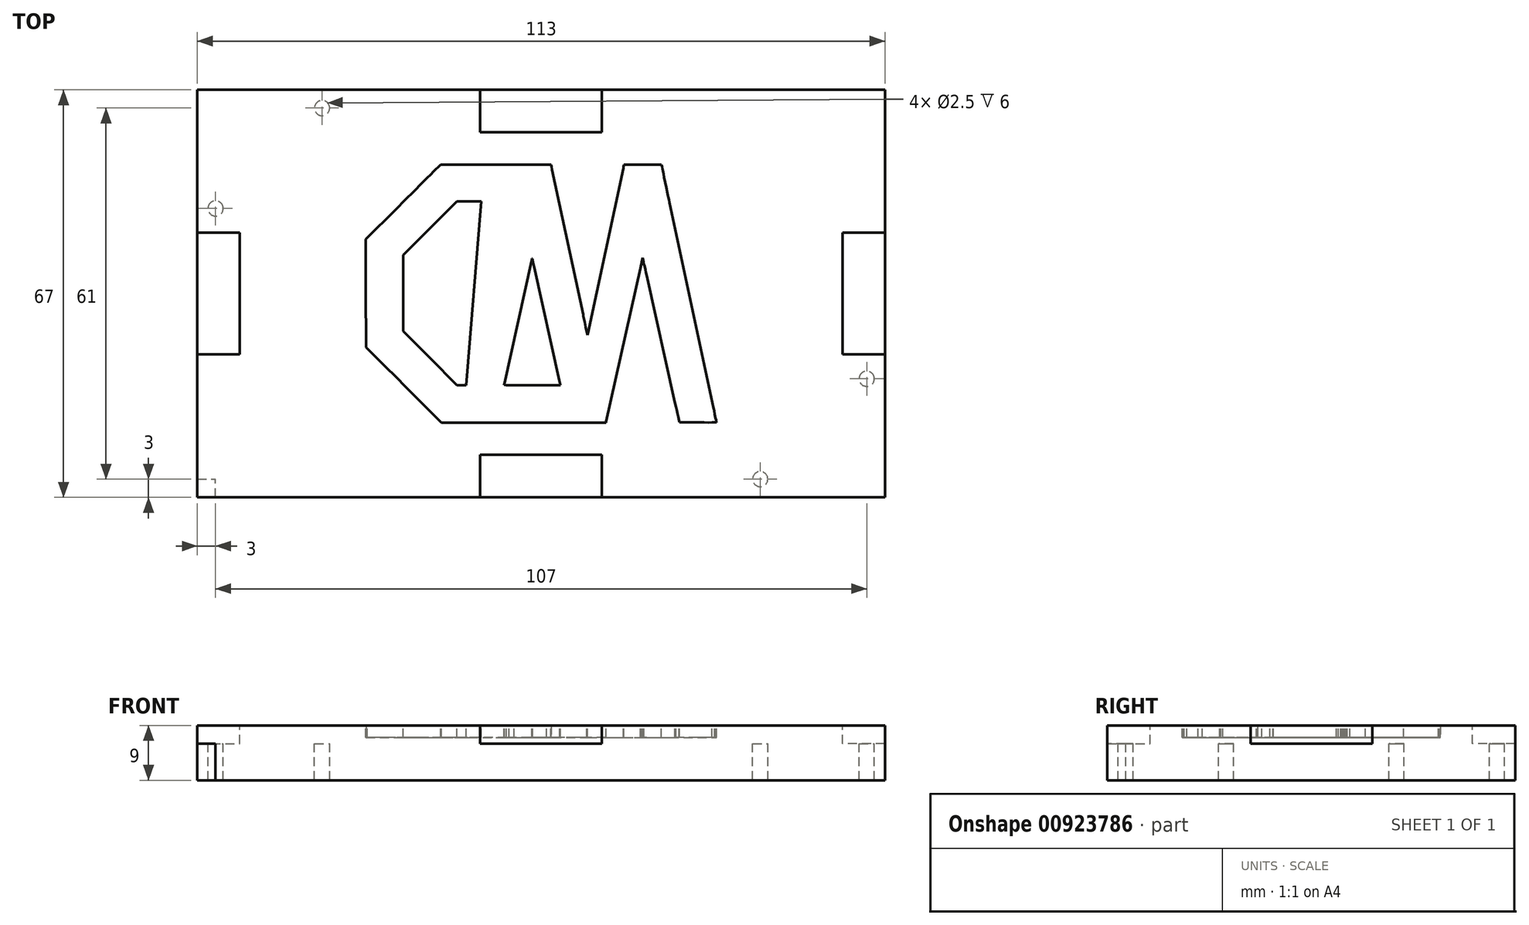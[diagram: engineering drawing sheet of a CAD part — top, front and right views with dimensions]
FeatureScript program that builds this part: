
annotation { "Feature Type Name" : "Feature", "Feature Type Description" : "" }
export const myFeature = defineFeature(function(context is Context, id is Id, definition is map)
    precondition{}
    {
        {
            var Q0;
            Q0=qCreatedBy(makeId("Top.planeOp"),FACE);
            var sketch = newSketch(context, id + "F0", { "sketchPlane" : qUnion([Q0])});
            skLineSegment(sketch, "E0.bottom", {"start": v(-56.5, 33.5) * mm, "end": v(56.5, 33.5) * mm});
            skLineSegment(sketch, "E0.top", {"start": v(-56.5, -33.5) * mm, "end": v(56.5, -33.5) * mm});
            skLineSegment(sketch, "E0.left", {"start": v(-56.5, 33.5) * mm, "end": v(-56.5, -33.5) * mm});
            skLineSegment(sketch, "E0.right", {"start": v(56.5, 33.5) * mm, "end": v(56.5, -33.5) * mm});
            skPoint(sketch, "E0.middle", {"position": v(0, 0) * mm});
            skSolve(sketch);
        }
        {
            var Q0;
            Q0=qSketchRegion(id+"F0",true);
            extrude(context, id + "F1", {"entities" : qUnion([Q0]), "depth" : 3 * mm, "offsetDistance" : 25 * mm});
        }
        {
            var Q0;
            Q0=makeQuery(id+"F1.opExtrude","CAP_FACE",FACE,{"disambiguationData":[OSD([sQuery(id+"F0.wireOp",EDGE,"E0.bottom"),sQuery(id+"F0.wireOp",EDGE,"E0.top"),sQuery(id+"F0.wireOp",EDGE,"E0.left"),sQuery(id+"F0.wireOp",EDGE,"E0.right")])],"isStart":true});
            var sketch = newSketch(context, id + "F2", { "sketchPlane" : qUnion([Q0])});
            skCircle(sketch, "E1", {"center": v(-36, 30.5) * mm, "radius": 1.25 * mm});
            skCircle(sketch, "E2.MirrorC", {"center": v(36, 30.5) * mm, "radius": 1.25 * mm});
            skCircle(sketch, "E3.MirrorC", {"center": v(-36, -30.5) * mm, "radius": 1.25 * mm});
            skCircle(sketch, "E4.MirrorC", {"center": v(36, -30.5) * mm, "radius": 1.25 * mm});
            skCircle(sketch, "E5", {"center": v(-53.5, 14) * mm, "radius": 1.25 * mm});
            skCircle(sketch, "E6.MirrorC", {"center": v(-53.5, -14) * mm, "radius": 1.25 * mm});
            skCircle(sketch, "E7.MirrorC", {"center": v(53.5, 14) * mm, "radius": 1.25 * mm});
            skCircle(sketch, "E8.MirrorC", {"center": v(53.5, -14) * mm, "radius": 1.25 * mm});
            skLineSegment(sketch, "E9", {"start": v(-56.5, 33.5) * mm, "end": v(-56.5, 30.5) * mm});
            skLineSegment(sketch, "E10.MirrorCS", {"start": v(56.5, 33.5) * mm, "end": v(56.5, 30.5) * mm});
            skLineSegment(sketch, "E11", {"start": v(-56.5, 30.5) * mm, "end": v(56.5, 30.5) * mm});
            skLineSegment(sketch, "E12", {"start": v(-56.5, 33.5) * mm, "end": v(-53.5, 33.5) * mm});
            skLineSegment(sketch, "E13.MirrorCS", {"start": v(-56.5, -33.5) * mm, "end": v(-53.5, -33.5) * mm});
            skLineSegment(sketch, "E14", {"start": v(-53.5, 33.5) * mm, "end": v(-53.5, -33.5) * mm});
            skSolve(sketch);
        }
        {
            var Q0;
            Q0=makeQuery(id+"F2.imprint","IMPRINT",FACE,{"disambiguationData":[TD([[makeQuery(id+"F2.imprint","IMPRINT",EDGE,{"derivedFrom":sQuery(id+"F2.wireOp",EDGE,"E5")}),1.0]])]});
            var Q1;
            Q1=makeQuery(id+"F2.imprint","IMPRINT",FACE,{"disambiguationData":[TD([[makeQuery(id+"F2.imprint","IMPRINT",EDGE,{"derivedFrom":sQuery(id+"F2.wireOp",EDGE,"E1")}),1.0]])]});
            var Q2;
            Q2=makeQuery(id+"F2.imprint","IMPRINT",FACE,{"disambiguationData":[TD([[makeQuery(id+"F2.imprint","IMPRINT",EDGE,{"derivedFrom":sQuery(id+"F2.wireOp",EDGE,"09FGcPzo-r08X-NdcF-ZMil-9gokYAyHGJ6w")}),1.0]])]});
            var Q3;
            Q3=makeQuery(id+"F2.imprint","IMPRINT",FACE,{"disambiguationData":[TD([[makeQuery(id+"F2.imprint","IMPRINT",EDGE,{"derivedFrom":sQuery(id+"F2.wireOp",EDGE,"6b634f44-071d-4c88-9b46-4b31445dddd10.MirrorC")}),-1.0]])]});
            var Q4;
            Q4=makeQuery(id+"F2.imprint","IMPRINT",FACE,{"disambiguationData":[TD([[makeQuery(id+"F2.imprint","IMPRINT",EDGE,{"derivedFrom":sQuery(id+"F2.wireOp",EDGE,"E2.MirrorC")}),-1.0]])]});
            var Q5;
            Q5=makeQuery(id+"F2.imprint","IMPRINT",FACE,{"disambiguationData":[TD([[makeQuery(id+"F2.imprint","IMPRINT",EDGE,{"derivedFrom":sQuery(id+"F2.wireOp",EDGE,"E7.MirrorC")}),-1.0]])]});
            var Q6;
            Q6=makeQuery(id+"F2.imprint","IMPRINT",FACE,{"disambiguationData":[TD([[makeQuery(id+"F2.imprint","IMPRINT",EDGE,{"derivedFrom":sQuery(id+"F2.wireOp",EDGE,"E8.MirrorC")}),1.0]])]});
            var Q7;
            Q7=makeQuery(id+"F2.imprint","IMPRINT",FACE,{"disambiguationData":[TD([[makeQuery(id+"F2.imprint","IMPRINT",EDGE,{"derivedFrom":sQuery(id+"F2.wireOp",EDGE,"E4.MirrorC")}),1.0]])]});
            var Q8;
            Q8=makeQuery(id+"F2.imprint","IMPRINT",FACE,{"disambiguationData":[TD([[makeQuery(id+"F2.imprint","IMPRINT",EDGE,{"derivedFrom":sQuery(id+"F2.wireOp",EDGE,"2bea74fb-fcac-444e-aa72-05c954cefff90.MirrorC")}),1.0]])]});
            var Q9;
            Q9=makeQuery(id+"F2.imprint","IMPRINT",FACE,{"disambiguationData":[TD([[makeQuery(id+"F2.imprint","IMPRINT",EDGE,{"derivedFrom":sQuery(id+"F2.wireOp",EDGE,"93892151-f29d-4d39-a853-46f32f35b9700.MirrorC")}),-1.0]])]});
            var Q10;
            Q10=makeQuery(id+"F2.imprint","IMPRINT",FACE,{"disambiguationData":[TD([[makeQuery(id+"F2.imprint","IMPRINT",EDGE,{"derivedFrom":sQuery(id+"F2.wireOp",EDGE,"E3.MirrorC")}),-1.0]])]});
            var Q11;
            Q11=makeQuery(id+"F2.imprint","IMPRINT",FACE,{"disambiguationData":[TD([[makeQuery(id+"F2.imprint","IMPRINT",EDGE,{"derivedFrom":sQuery(id+"F2.wireOp",EDGE,"E6.MirrorC")}),-1.0]])]});
            extrude(context, id + "F3", {"entities" : qUnion([Q0, Q1, Q2, Q3, Q4, Q5, Q6, Q7, Q8, Q9, Q10, Q11]), "operationType" : NewBodyOperationType.ADD, "depth" : 6 * mm, "offsetDistance" : 25 * mm});
        }
        {
            var Q0;
            Q0=makeQuery(id+"F1.opExtrude","CAP_FACE",FACE,{"disambiguationData":[OSD([sQuery(id+"F0.wireOp",EDGE,"E0.bottom"),sQuery(id+"F0.wireOp",EDGE,"E0.top"),sQuery(id+"F0.wireOp",EDGE,"E0.left"),sQuery(id+"F0.wireOp",EDGE,"E0.right")])],"isStart":false});
            var sketch = newSketch(context, id + "F4", { "sketchPlane" : qUnion([Q0])});
            skLineSegment(sketch, "E15", {"start": v(-10, 33.5) * mm, "end": v(10, 33.5) * mm});
            skLineSegment(sketch, "E16", {"start": v(-10, 33.5) * mm, "end": v(-10, 26.5) * mm});
            skLineSegment(sketch, "E17", {"start": v(-10, 26.5) * mm, "end": v(10, 26.5) * mm});
            skLineSegment(sketch, "E18", {"start": v(10, 26.5) * mm, "end": v(10, 33.5) * mm});
            skLineSegment(sketch, "E19.MirrorCS", {"start": v(-10, -33.5) * mm, "end": v(-10, -26.5) * mm});
            skLineSegment(sketch, "E20.MirrorCS", {"start": v(-10, -26.5) * mm, "end": v(10, -26.5) * mm});
            skLineSegment(sketch, "E21.MirrorCS", {"start": v(10, -26.5) * mm, "end": v(10, -33.5) * mm});
            skLineSegment(sketch, "E22.MirrorCS", {"start": v(-10, -33.5) * mm, "end": v(10, -33.5) * mm});
            skLineSegment(sketch, "E23", {"start": v(-56.5, 10) * mm, "end": v(-56.5, -10) * mm});
            skLineSegment(sketch, "E24", {"start": v(-56.5, 10) * mm, "end": v(-49.5, 10) * mm});
            skLineSegment(sketch, "E25", {"start": v(-49.5, 10) * mm, "end": v(-49.5, -10) * mm});
            skLineSegment(sketch, "E26", {"start": v(-49.5, -10) * mm, "end": v(-56.5, -10) * mm});
            skLineSegment(sketch, "E27.MirrorCS", {"start": v(56.5, 10) * mm, "end": v(49.5, 10) * mm});
            skLineSegment(sketch, "E28.MirrorCS", {"start": v(56.5, 10) * mm, "end": v(56.5, -10) * mm});
            skLineSegment(sketch, "E29.MirrorCS", {"start": v(49.5, -10) * mm, "end": v(56.5, -10) * mm});
            skLineSegment(sketch, "E30.MirrorCS", {"start": v(49.5, 10) * mm, "end": v(49.5, -10) * mm});
            skSolve(sketch);
        }
        {
            var Q0;
            Q0=makeQuery(id+"F4.imprint","IMPRINT",FACE,{"disambiguationData":[TD([[makeQuery(id+"F4.imprint","IMPRINT",EDGE,{"derivedFrom":sQuery(id+"F4.wireOp",EDGE,"E23")}),1.0]])]});
            var Q1;
            Q1=makeQuery(id+"F4.imprint","IMPRINT",FACE,{"disambiguationData":[TD([[makeQuery(id+"F4.imprint","IMPRINT",EDGE,{"derivedFrom":sQuery(id+"F4.wireOp",EDGE,"E15")}),-1.0]])]});
            var Q2;
            Q2=makeQuery(id+"F4.imprint","IMPRINT",FACE,{"disambiguationData":[TD([[makeQuery(id+"F4.imprint","IMPRINT",EDGE,{"derivedFrom":sQuery(id+"F4.wireOp",EDGE,"E27.MirrorCS")}),1.0]])]});
            var Q3;
            Q3=makeQuery(id+"F4.imprint","IMPRINT",FACE,{"disambiguationData":[TD([[makeQuery(id+"F4.imprint","IMPRINT",EDGE,{"derivedFrom":sQuery(id+"F4.wireOp",EDGE,"E19.MirrorCS")}),-1.0]])]});
            extrude(context, id + "F5", {"entities" : qUnion([Q0, Q1, Q2, Q3]), "operationType" : NewBodyOperationType.REMOVE, "oppositeDirection" : true, "depth" : 3 * mm, "offsetDistance" : 25 * mm});
        }
        {
            var Q0;
            Q0=makeQuery(id+"F1.opExtrude","CAP_FACE",FACE,{"disambiguationData":[OSD([sQuery(id+"F0.wireOp",EDGE,"E0.bottom"),sQuery(id+"F0.wireOp",EDGE,"E0.top"),sQuery(id+"F0.wireOp",EDGE,"E0.left"),sQuery(id+"F0.wireOp",EDGE,"E0.right")])],"isStart":false});
            var sketch = newSketch(context, id + "F6", { "sketchPlane" : qUnion([Q0])});
            skLineSegment(sketch, "E31", {"start": v(-13.82, -15.06) * mm, "end": v(-12.3, -15.06) * mm});
            skLineSegment(sketch, "E32", {"start": v(-18.24, -10.63) * mm, "end": v(-13.82, -15.06) * mm});
            skLineSegment(sketch, "E33", {"start": v(-22.67, -6.2) * mm, "end": v(-18.24, -10.63) * mm});
            skLineSegment(sketch, "E34", {"start": v(-22.67, -6.2) * mm, "end": v(-22.66, 6.32) * mm});
            skLineSegment(sketch, "E35", {"start": v(-18.26, 10.74) * mm, "end": v(-22.66, 6.32) * mm});
            skLineSegment(sketch, "E36", {"start": v(-13.86, 15.17) * mm, "end": v(-18.26, 10.74) * mm});
            skLineSegment(sketch, "E37", {"start": v(-9.85, 15.17) * mm, "end": v(-13.86, 15.17) * mm});
            skLineSegment(sketch, "E38", {"start": v(-12.3, -15.06) * mm, "end": v(-9.85, 15.17) * mm});
            skLineSegment(sketch, "E39", {"start": v(-6.04, -14.81) * mm, "end": v(-6.07, -14.95) * mm});
            skLineSegment(sketch, "E40", {"start": v(-6.07, -14.95) * mm, "end": v(-6.08, -15.01) * mm});
            skLineSegment(sketch, "E41", {"start": v(-6.04, -14.81) * mm, "end": v(-1.56, 5.34) * mm});
            skLineSegment(sketch, "E42", {"start": v(-1.5, 5.66) * mm, "end": v(-1.53, 5.51) * mm});
            skLineSegment(sketch, "E43", {"start": v(-1.53, 5.51) * mm, "end": v(-1.56, 5.34) * mm});
            skLineSegment(sketch, "E44", {"start": v(-1.4, 5.57) * mm, "end": v(-1.44, 5.72) * mm});
            skLineSegment(sketch, "E45", {"start": v(-1.44, 5.72) * mm, "end": v(-1.48, 5.78) * mm});
            skLineSegment(sketch, "E46", {"start": v(-1.48, 5.78) * mm, "end": v(-1.49, 5.78) * mm});
            skLineSegment(sketch, "E47", {"start": v(-1.49, 5.78) * mm, "end": v(-1.5, 5.76) * mm});
            skLineSegment(sketch, "E48", {"start": v(-1.5, 5.76) * mm, "end": v(-1.5, 5.66) * mm});
            skLineSegment(sketch, "E49", {"start": v(-1.14, 4.4) * mm, "end": v(-1.3, 5.12) * mm});
            skLineSegment(sketch, "E50", {"start": v(-1.3, 5.12) * mm, "end": v(-1.4, 5.57) * mm});
            skLineSegment(sketch, "E51", {"start": v(3, -14.3) * mm, "end": v(-1.14, 4.4) * mm});
            skLineSegment(sketch, "E52", {"start": v(3.13, -14.84) * mm, "end": v(3.06, -14.55) * mm});
            skLineSegment(sketch, "E53", {"start": v(3.06, -14.55) * mm, "end": v(3, -14.3) * mm});
            skLineSegment(sketch, "E54", {"start": v(3.19, -15.06) * mm, "end": v(3.13, -14.84) * mm});
            skLineSegment(sketch, "E55", {"start": v(0.11, -15.06) * mm, "end": v(3.19, -15.06) * mm});
            skLineSegment(sketch, "E56", {"start": v(-3.62, -15.07) * mm, "end": v(-3.3, -15.07) * mm});
            skLineSegment(sketch, "E57", {"start": v(-3.3, -15.07) * mm, "end": v(-2.73, -15.07) * mm});
            skLineSegment(sketch, "E58", {"start": v(-2.73, -15.07) * mm, "end": v(-2, -15.06) * mm});
            skLineSegment(sketch, "E59", {"start": v(-2, -15.06) * mm, "end": v(-1, -15.06) * mm});
            skLineSegment(sketch, "E60", {"start": v(-1, -15.06) * mm, "end": v(0.11, -15.06) * mm});
            skLineSegment(sketch, "E61", {"start": v(-6.08, -15.01) * mm, "end": v(-6.07, -15.02) * mm});
            skLineSegment(sketch, "E62", {"start": v(-6.07, -15.02) * mm, "end": v(-6.06, -15.02) * mm});
            skLineSegment(sketch, "E63", {"start": v(-6.06, -15.02) * mm, "end": v(-6.02, -15.03) * mm});
            skLineSegment(sketch, "E64", {"start": v(-6.02, -15.03) * mm, "end": v(-5.73, -15.05) * mm});
            skLineSegment(sketch, "E65", {"start": v(-5.73, -15.05) * mm, "end": v(-5.27, -15.07) * mm});
            skLineSegment(sketch, "E66", {"start": v(-5.27, -15.07) * mm, "end": v(-4.47, -15.08) * mm});
            skLineSegment(sketch, "E67", {"start": v(-4.47, -15.08) * mm, "end": v(-3.62, -15.07) * mm});
            skLineSegment(sketch, "E68", {"start": v(16.62, 5.68) * mm, "end": v(16.57, 5.4) * mm});
            skLineSegment(sketch, "E69", {"start": v(16.57, 5.4) * mm, "end": v(16.53, 5.24) * mm});
            skLineSegment(sketch, "E70", {"start": v(16.7, 5.9) * mm, "end": v(16.7, 5.91) * mm});
            skLineSegment(sketch, "E71", {"start": v(16.7, 5.91) * mm, "end": v(16.69, 5.91) * mm});
            skLineSegment(sketch, "E72", {"start": v(16.69, 5.91) * mm, "end": v(16.68, 5.9) * mm});
            skLineSegment(sketch, "E73", {"start": v(16.68, 5.9) * mm, "end": v(16.62, 5.68) * mm});
            skLineSegment(sketch, "E74", {"start": v(16.8, 5.5) * mm, "end": v(16.73, 5.8) * mm});
            skLineSegment(sketch, "E75", {"start": v(16.73, 5.8) * mm, "end": v(16.7, 5.88) * mm});
            skLineSegment(sketch, "E76", {"start": v(16.7, 5.88) * mm, "end": v(16.7, 5.9) * mm});
            skLineSegment(sketch, "E77", {"start": v(16.7, 5.9) * mm, "end": v(16.7, 5.9) * mm});
            skLineSegment(sketch, "E78", {"start": v(16.93, 4.84) * mm, "end": v(16.85, 5.19) * mm});
            skLineSegment(sketch, "E79", {"start": v(16.85, 5.19) * mm, "end": v(16.8, 5.5) * mm});
            skLineSegment(sketch, "E80", {"start": v(17.12, 3.95) * mm, "end": v(17, 4.52) * mm});
            skLineSegment(sketch, "E81", {"start": v(17, 4.52) * mm, "end": v(16.93, 4.84) * mm});
            skLineSegment(sketch, "E82", {"start": v(17.32, 3.06) * mm, "end": v(17.22, 3.5) * mm});
            skLineSegment(sketch, "E83", {"start": v(17.22, 3.5) * mm, "end": v(17.12, 3.95) * mm});
            skLineSegment(sketch, "E84", {"start": v(17.32, 3.06) * mm, "end": v(21.98, -17.92) * mm});
            skLineSegment(sketch, "E85", {"start": v(22.41, -19.78) * mm, "end": v(22.26, -19.1) * mm});
            skLineSegment(sketch, "E86", {"start": v(22.26, -19.1) * mm, "end": v(22.15, -18.6) * mm});
            skLineSegment(sketch, "E87", {"start": v(22.15, -18.6) * mm, "end": v(21.98, -17.92) * mm});
            skLineSegment(sketch, "E88", {"start": v(22.7, -21.07) * mm, "end": v(22.67, -20.91) * mm});
            skLineSegment(sketch, "E89", {"start": v(22.67, -20.91) * mm, "end": v(22.6, -20.61) * mm});
            skLineSegment(sketch, "E90", {"start": v(22.6, -20.61) * mm, "end": v(22.52, -20.26) * mm});
            skLineSegment(sketch, "E91", {"start": v(22.52, -20.26) * mm, "end": v(22.41, -19.78) * mm});
            skLineSegment(sketch, "E92", {"start": v(22.74, -21.18) * mm, "end": v(22.7, -21.07) * mm});
            skLineSegment(sketch, "E93", {"start": v(25.77, -21.19) * mm, "end": v(22.74, -21.18) * mm});
            skLineSegment(sketch, "E94", {"start": v(28.8, -21.11) * mm, "end": v(28.8, -21.14) * mm});
            skLineSegment(sketch, "E95", {"start": v(28.8, -21.14) * mm, "end": v(28.76, -21.16) * mm});
            skLineSegment(sketch, "E96", {"start": v(28.76, -21.16) * mm, "end": v(28.5, -21.18) * mm});
            skLineSegment(sketch, "E97", {"start": v(28.5, -21.18) * mm, "end": v(28.06, -21.2) * mm});
            skLineSegment(sketch, "E98", {"start": v(28.06, -21.2) * mm, "end": v(27.52, -21.2) * mm});
            skLineSegment(sketch, "E99", {"start": v(27.52, -21.2) * mm, "end": v(26.77, -21.2) * mm});
            skLineSegment(sketch, "E100", {"start": v(26.77, -21.2) * mm, "end": v(25.77, -21.19) * mm});
            skLineSegment(sketch, "E101", {"start": v(28.74, -20.79) * mm, "end": v(28.8, -21) * mm});
            skLineSegment(sketch, "E102", {"start": v(28.8, -21) * mm, "end": v(28.8, -21.11) * mm});
            skLineSegment(sketch, "E103", {"start": v(28.53, -19.8) * mm, "end": v(28.67, -20.46) * mm});
            skLineSegment(sketch, "E104", {"start": v(28.67, -20.46) * mm, "end": v(28.74, -20.79) * mm});
            skLineSegment(sketch, "E105", {"start": v(28.32, -18.79) * mm, "end": v(28.36, -18.98) * mm});
            skLineSegment(sketch, "E106", {"start": v(28.36, -18.98) * mm, "end": v(28.42, -19.26) * mm});
            skLineSegment(sketch, "E107", {"start": v(28.42, -19.26) * mm, "end": v(28.53, -19.8) * mm});
            skLineSegment(sketch, "E108", {"start": v(21.1, 14.95) * mm, "end": v(28.32, -18.79) * mm});
            skLineSegment(sketch, "E109", {"start": v(20.9, 15.85) * mm, "end": v(21, 15.41) * mm});
            skLineSegment(sketch, "E110", {"start": v(21, 15.41) * mm, "end": v(21.1, 14.95) * mm});
            skLineSegment(sketch, "E111", {"start": v(20.79, 16.43) * mm, "end": v(20.85, 16.1) * mm});
            skLineSegment(sketch, "E112", {"start": v(20.85, 16.1) * mm, "end": v(20.9, 15.85) * mm});
            skLineSegment(sketch, "E113", {"start": v(20.1, 19.65) * mm, "end": v(20.21, 19.1) * mm});
            skLineSegment(sketch, "E114", {"start": v(20.21, 19.1) * mm, "end": v(20.39, 18.3) * mm});
            skLineSegment(sketch, "E115", {"start": v(20.39, 18.3) * mm, "end": v(20.57, 17.45) * mm});
            skLineSegment(sketch, "E116", {"start": v(20.57, 17.45) * mm, "end": v(20.79, 16.43) * mm});
            skLineSegment(sketch, "E117", {"start": v(19.97, 20.25) * mm, "end": v(20.04, 19.92) * mm});
            skLineSegment(sketch, "E118", {"start": v(20.04, 19.92) * mm, "end": v(20.1, 19.65) * mm});
            skLineSegment(sketch, "E119", {"start": v(19.85, 20.87) * mm, "end": v(19.92, 20.5) * mm});
            skLineSegment(sketch, "E120", {"start": v(19.92, 20.5) * mm, "end": v(19.97, 20.25) * mm});
            skLineSegment(sketch, "E121", {"start": v(19.78, 21.22) * mm, "end": v(19.85, 20.87) * mm});
            skLineSegment(sketch, "E122", {"start": v(13.61, 21.22) * mm, "end": v(19.78, 21.22) * mm});
            skLineSegment(sketch, "E123", {"start": v(13.58, 21.06) * mm, "end": v(13.61, 21.22) * mm});
            skLineSegment(sketch, "E124", {"start": v(13.5, 20.65) * mm, "end": v(13.55, 20.9) * mm});
            skLineSegment(sketch, "E125", {"start": v(13.55, 20.9) * mm, "end": v(13.58, 21.06) * mm});
            skLineSegment(sketch, "E126", {"start": v(7.67, -6.57) * mm, "end": v(13.5, 20.65) * mm});
            skLineSegment(sketch, "E127", {"start": v(7.61, -6.83) * mm, "end": v(7.67, -6.57) * mm});
            skLineSegment(sketch, "E128", {"start": v(7.56, -6.55) * mm, "end": v(7.61, -6.83) * mm});
            skLineSegment(sketch, "E129", {"start": v(7.45, -6.02) * mm, "end": v(7.51, -6.32) * mm});
            skLineSegment(sketch, "E130", {"start": v(7.51, -6.32) * mm, "end": v(7.56, -6.55) * mm});
            skLineSegment(sketch, "E131", {"start": v(7.33, -5.45) * mm, "end": v(7.4, -5.79) * mm});
            skLineSegment(sketch, "E132", {"start": v(7.4, -5.79) * mm, "end": v(7.45, -6.02) * mm});
            skLineSegment(sketch, "E133", {"start": v(6.9, -3.42) * mm, "end": v(6.96, -3.71) * mm});
            skLineSegment(sketch, "E134", {"start": v(6.96, -3.71) * mm, "end": v(7.06, -4.18) * mm});
            skLineSegment(sketch, "E135", {"start": v(7.06, -4.18) * mm, "end": v(7.17, -4.72) * mm});
            skLineSegment(sketch, "E136", {"start": v(7.17, -4.72) * mm, "end": v(7.33, -5.45) * mm});
            skLineSegment(sketch, "E137", {"start": v(1.8, 20.35) * mm, "end": v(6.9, -3.42) * mm});
            skLineSegment(sketch, "E138", {"start": v(1.63, 21.19) * mm, "end": v(1.63, 21.18) * mm});
            skLineSegment(sketch, "E139", {"start": v(1.63, 21.18) * mm, "end": v(1.63, 21.17) * mm});
            skLineSegment(sketch, "E140", {"start": v(1.63, 21.17) * mm, "end": v(1.63, 21.15) * mm});
            skLineSegment(sketch, "E141", {"start": v(1.63, 21.15) * mm, "end": v(1.65, 21.07) * mm});
            skLineSegment(sketch, "E142", {"start": v(1.65, 21.07) * mm, "end": v(1.7, 20.87) * mm});
            skLineSegment(sketch, "E143", {"start": v(1.7, 20.87) * mm, "end": v(1.8, 20.35) * mm});
            skLineSegment(sketch, "E144", {"start": v(-7.44, 21.22) * mm, "end": v(0.91, 21.2) * mm});
            skLineSegment(sketch, "E145", {"start": v(0.91, 21.2) * mm, "end": v(1.58, 21.2) * mm});
            skLineSegment(sketch, "E146", {"start": v(1.58, 21.2) * mm, "end": v(1.62, 21.19) * mm});
            skLineSegment(sketch, "E147", {"start": v(1.62, 21.19) * mm, "end": v(1.63, 21.19) * mm});
            skLineSegment(sketch, "E148", {"start": v(1.63, 21.19) * mm, "end": v(1.63, 21.19) * mm});
            skLineSegment(sketch, "E149", {"start": v(-16.52, 21.22) * mm, "end": v(-7.44, 21.22) * mm});
            skLineSegment(sketch, "E150", {"start": v(-17.7, 20.03) * mm, "end": v(-16.52, 21.22) * mm});
            skLineSegment(sketch, "E151", {"start": v(-23.84, 13.88) * mm, "end": v(-22.32, 15.4) * mm});
            skLineSegment(sketch, "E152", {"start": v(-22.32, 15.4) * mm, "end": v(-20.88, 16.84) * mm});
            skLineSegment(sketch, "E153", {"start": v(-20.88, 16.84) * mm, "end": v(-19.6, 18.12) * mm});
            skLineSegment(sketch, "E154", {"start": v(-19.6, 18.12) * mm, "end": v(-18.76, 18.96) * mm});
            skLineSegment(sketch, "E155", {"start": v(-18.76, 18.96) * mm, "end": v(-18.12, 19.61) * mm});
            skLineSegment(sketch, "E156", {"start": v(-18.12, 19.61) * mm, "end": v(-17.7, 20.03) * mm});
            skLineSegment(sketch, "E157", {"start": v(-28.8, 8.92) * mm, "end": v(-23.84, 13.88) * mm});
            skLineSegment(sketch, "E158", {"start": v(-28.8, 0.04) * mm, "end": v(-28.8, 8.92) * mm});
            skLineSegment(sketch, "E159", {"start": v(-28.78, -8.84) * mm, "end": v(-28.78, -8.84) * mm});
            skLineSegment(sketch, "E160", {"start": v(-28.78, -8.84) * mm, "end": v(-28.78, -8.83) * mm});
            skLineSegment(sketch, "E161", {"start": v(-28.78, -8.83) * mm, "end": v(-28.78, -8.8) * mm});
            skLineSegment(sketch, "E162", {"start": v(-28.78, -8.8) * mm, "end": v(-28.8, -8.14) * mm});
            skLineSegment(sketch, "E163", {"start": v(-28.8, -8.14) * mm, "end": v(-28.8, 0.04) * mm});
            skLineSegment(sketch, "E164", {"start": v(-20.04, -17.54) * mm, "end": v(-22.15, -15.42) * mm});
            skLineSegment(sketch, "E165", {"start": v(-22.15, -15.42) * mm, "end": v(-23.96, -13.62) * mm});
            skLineSegment(sketch, "E166", {"start": v(-23.96, -13.62) * mm, "end": v(-25.46, -12.12) * mm});
            skLineSegment(sketch, "E167", {"start": v(-25.46, -12.12) * mm, "end": v(-26.67, -10.91) * mm});
            skLineSegment(sketch, "E168", {"start": v(-26.67, -10.91) * mm, "end": v(-27.6, -10) * mm});
            skLineSegment(sketch, "E169", {"start": v(-27.6, -10) * mm, "end": v(-28.25, -9.34) * mm});
            skLineSegment(sketch, "E170", {"start": v(-28.25, -9.34) * mm, "end": v(-28.57, -9.03) * mm});
            skLineSegment(sketch, "E171", {"start": v(-28.57, -9.03) * mm, "end": v(-28.74, -8.87) * mm});
            skLineSegment(sketch, "E172", {"start": v(-28.74, -8.87) * mm, "end": v(-28.77, -8.85) * mm});
            skLineSegment(sketch, "E173", {"start": v(-28.77, -8.85) * mm, "end": v(-28.78, -8.84) * mm});
            skLineSegment(sketch, "E174", {"start": v(-16.37, -21.22) * mm, "end": v(-20.04, -17.54) * mm});
            skLineSegment(sketch, "E175", {"start": v(-5.62, -21.22) * mm, "end": v(-16.37, -21.22) * mm});
            skLineSegment(sketch, "E176", {"start": v(7.88, -21.2) * mm, "end": v(6.99, -21.2) * mm});
            skLineSegment(sketch, "E177", {"start": v(6.99, -21.2) * mm, "end": v(5.64, -21.2) * mm});
            skLineSegment(sketch, "E178", {"start": v(5.64, -21.2) * mm, "end": v(3.9, -21.21) * mm});
            skLineSegment(sketch, "E179", {"start": v(3.9, -21.21) * mm, "end": v(1.87, -21.21) * mm});
            skLineSegment(sketch, "E180", {"start": v(1.87, -21.21) * mm, "end": v(-1.75, -21.22) * mm});
            skLineSegment(sketch, "E181", {"start": v(-1.75, -21.22) * mm, "end": v(-5.62, -21.22) * mm});
            skLineSegment(sketch, "E182", {"start": v(10.64, -21.2) * mm, "end": v(7.88, -21.2) * mm});
            skLineSegment(sketch, "E183", {"start": v(10.68, -21.04) * mm, "end": v(10.64, -21.2) * mm});
            skLineSegment(sketch, "E184", {"start": v(10.68, -21.04) * mm, "end": v(16.32, 4.16) * mm});
            skLineSegment(sketch, "E185", {"start": v(16.45, 4.82) * mm, "end": v(16.38, 4.47) * mm});
            skLineSegment(sketch, "E186", {"start": v(16.38, 4.47) * mm, "end": v(16.32, 4.16) * mm});
            skLineSegment(sketch, "E187", {"start": v(16.53, 5.24) * mm, "end": v(16.48, 5.02) * mm});
            skLineSegment(sketch, "E188", {"start": v(16.48, 5.02) * mm, "end": v(16.45, 4.82) * mm});
            skSolve(sketch);
        }
        {
            var Q0;
            Q0=makeQuery(id+"F6.imprint","IMPRINT",FACE,{"disambiguationData":[TD([[makeQuery(id+"F6.imprint","IMPRINT",EDGE,{"derivedFrom":sQuery(id+"F6.wireOp",EDGE,"E31")}),-1.0]])]});
            extrude(context, id + "F7", {"entities" : qUnion([Q0]), "operationType" : NewBodyOperationType.REMOVE, "oppositeDirection" : true, "depth" : 2 * mm, "offsetDistance" : 25 * mm});
        }
    });
